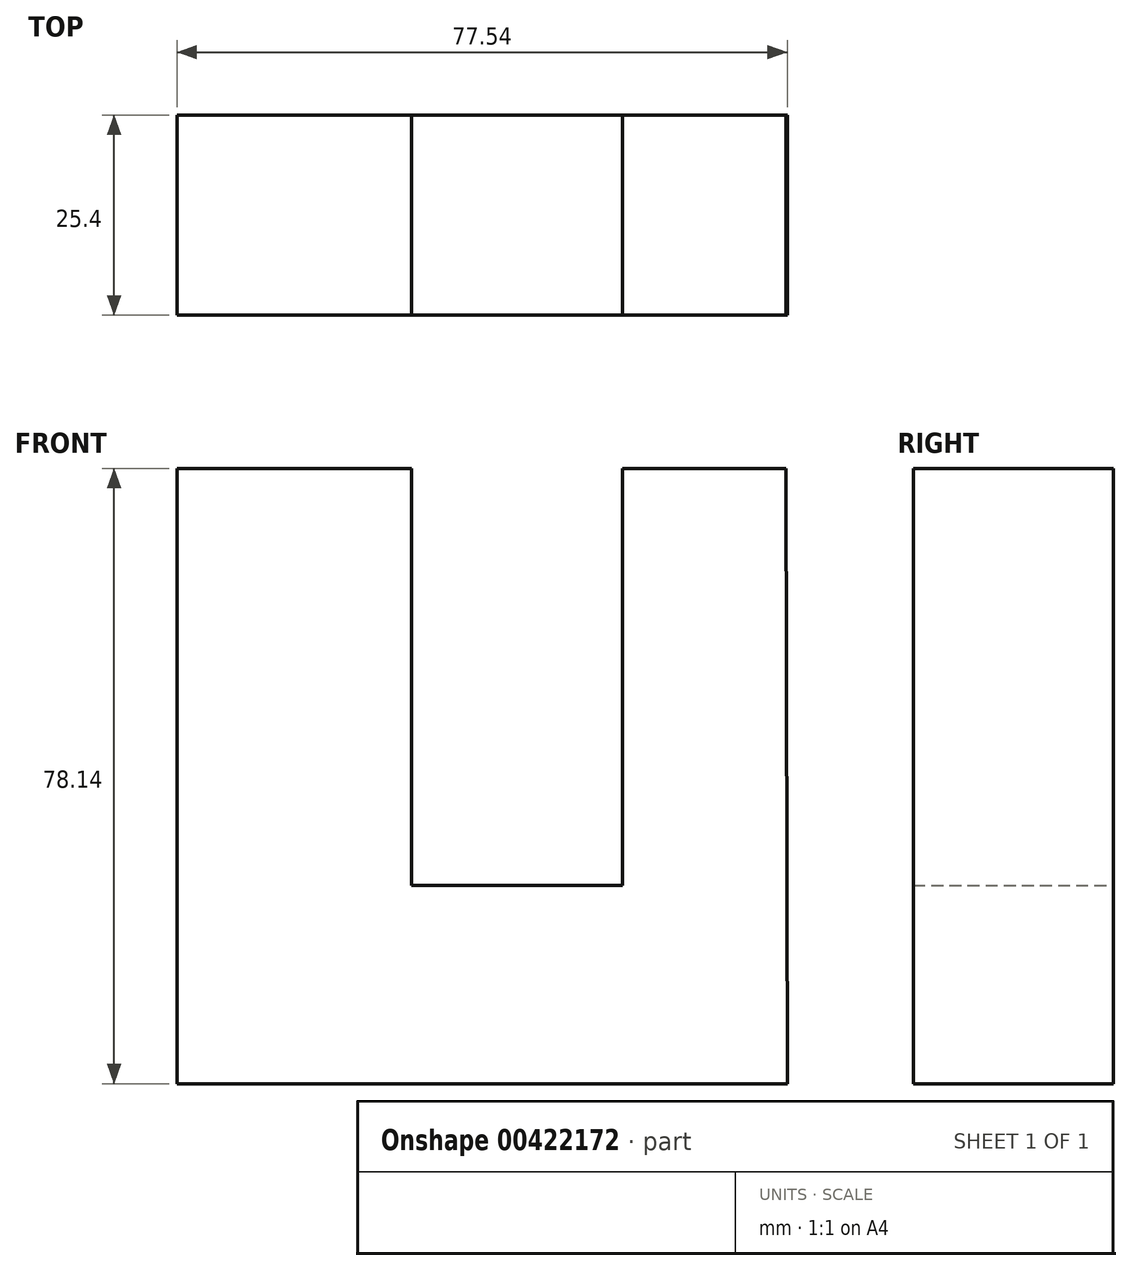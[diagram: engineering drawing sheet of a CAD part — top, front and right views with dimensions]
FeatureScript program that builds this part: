
annotation { "Feature Type Name" : "Feature", "Feature Type Description" : "" }
export const myFeature = defineFeature(function(context is Context, id is Id, definition is map)
    precondition{}
    {
        {
            var Q0;
            Q0=qCreatedBy(makeId("Front.planeOp"),FACE);
            var sketch = newSketch(context, id + "F0", { "sketchPlane" : qUnion([Q0])});
            skLineSegment(sketch, "E0", {"start": v(-74.68, 52.98) * mm, "end": v(-44.89, 52.98) * mm});
            skLineSegment(sketch, "E1", {"start": v(-74.68, 52.98) * mm, "end": v(-74.68, -25.16) * mm});
            skLineSegment(sketch, "E2", {"start": v(-74.68, -25.16) * mm, "end": v(2.86, -25.16) * mm});
            skLineSegment(sketch, "E3", {"start": v(-44.89, 52.98) * mm, "end": v(-44.89, 0) * mm});
            skLineSegment(sketch, "E4", {"start": v(-44.89, 0) * mm, "end": v(-18.05, 0) * mm});
            skLineSegment(sketch, "E5", {"start": v(-18.05, 0) * mm, "end": v(-18.05, 52.98) * mm});
            skPoint(sketch, "E6.end.orphan", {"position": v(0, 52.98) * mm});
            skLineSegment(sketch, "E7", {"start": v(-18.05, 52.98) * mm, "end": v(2.66, 52.98) * mm});
            skLineSegment(sketch, "E8", {"start": v(2.66, 52.98) * mm, "end": v(2.86, -25.16) * mm});
            skSolve(sketch);
        }
        {
            var Q0;
            Q0=makeQuery(id+"F0.imprint","IMPRINT",FACE,{"disambiguationData":[TD([[makeQuery(id+"F0.imprint","IMPRINT",EDGE,{"derivedFrom":sQuery(id+"F0.wireOp",EDGE,"E0")}),-1.0]])]});
            extrude(context, id + "F1", {"entities" : qUnion([Q0]), "depth" : 25.4 * mm});
        }
    });
